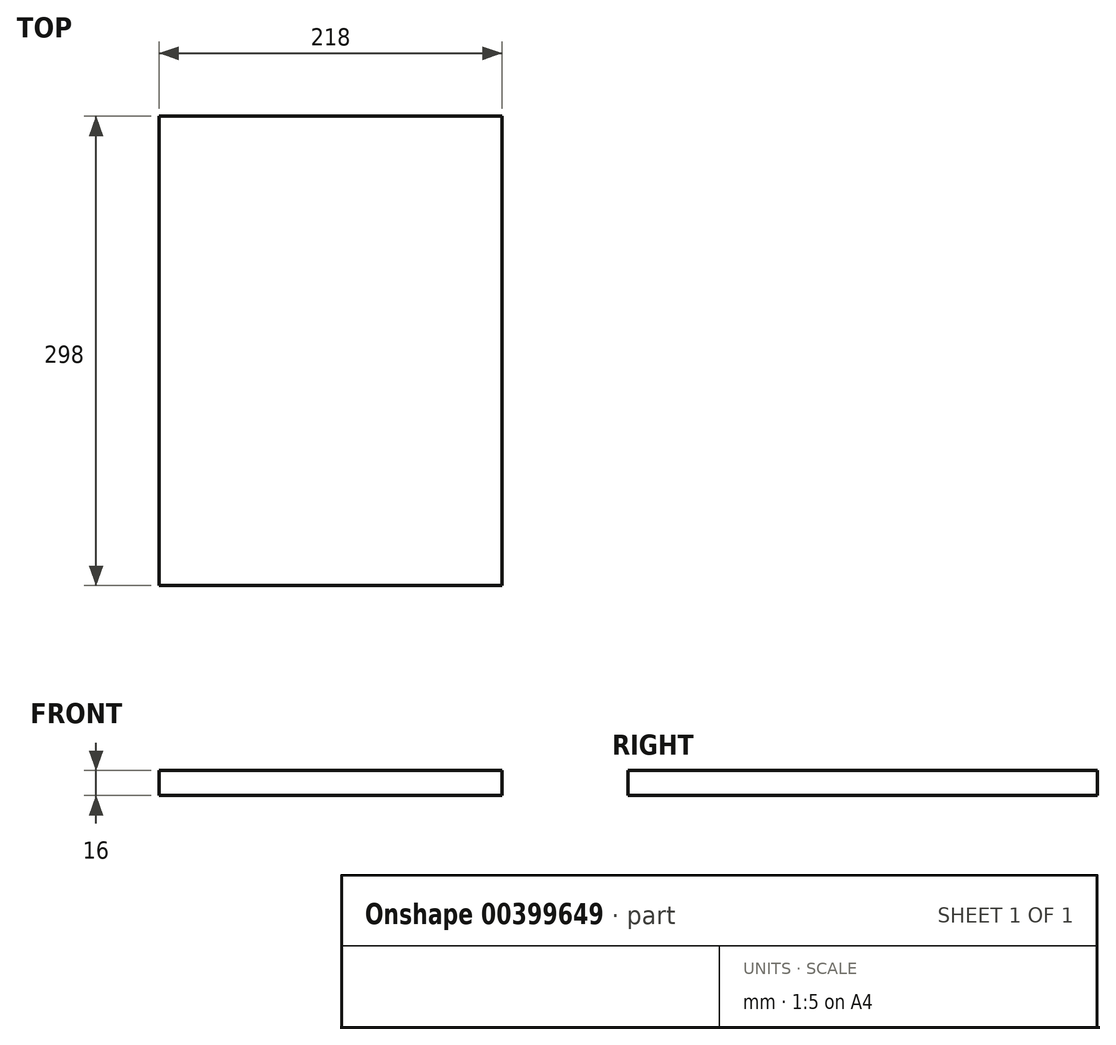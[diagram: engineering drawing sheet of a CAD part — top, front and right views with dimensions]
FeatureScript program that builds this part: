
annotation { "Feature Type Name" : "Feature", "Feature Type Description" : "" }
export const myFeature = defineFeature(function(context is Context, id is Id, definition is map)
    precondition{}
    {
        {
            var Q0;
            Q0=qCreatedBy(makeId("Top.planeOp"),FACE);
            var sketch = newSketch(context, id + "F0", { "sketchPlane" : qUnion([Q0])});
            skLineSegment(sketch, "E0.bottom", {"start": v(-109, 149) * mm, "end": v(109, 149) * mm});
            skLineSegment(sketch, "E0.top", {"start": v(-109, -149) * mm, "end": v(109, -149) * mm});
            skLineSegment(sketch, "E0.left", {"start": v(-109, 149) * mm, "end": v(-109, -149) * mm});
            skLineSegment(sketch, "E0.right", {"start": v(109, 149) * mm, "end": v(109, -149) * mm});
            skPoint(sketch, "E0.middle", {"position": v(0, 0) * mm});
            skSolve(sketch);
        }
        {
            var Q0;
            Q0 = qSketchRegion(id + "F0", true);
            extrude(context, id + "F1", {"entities" : qUnion([Q0]), "depth" : 16 * mm});
        }
    });
